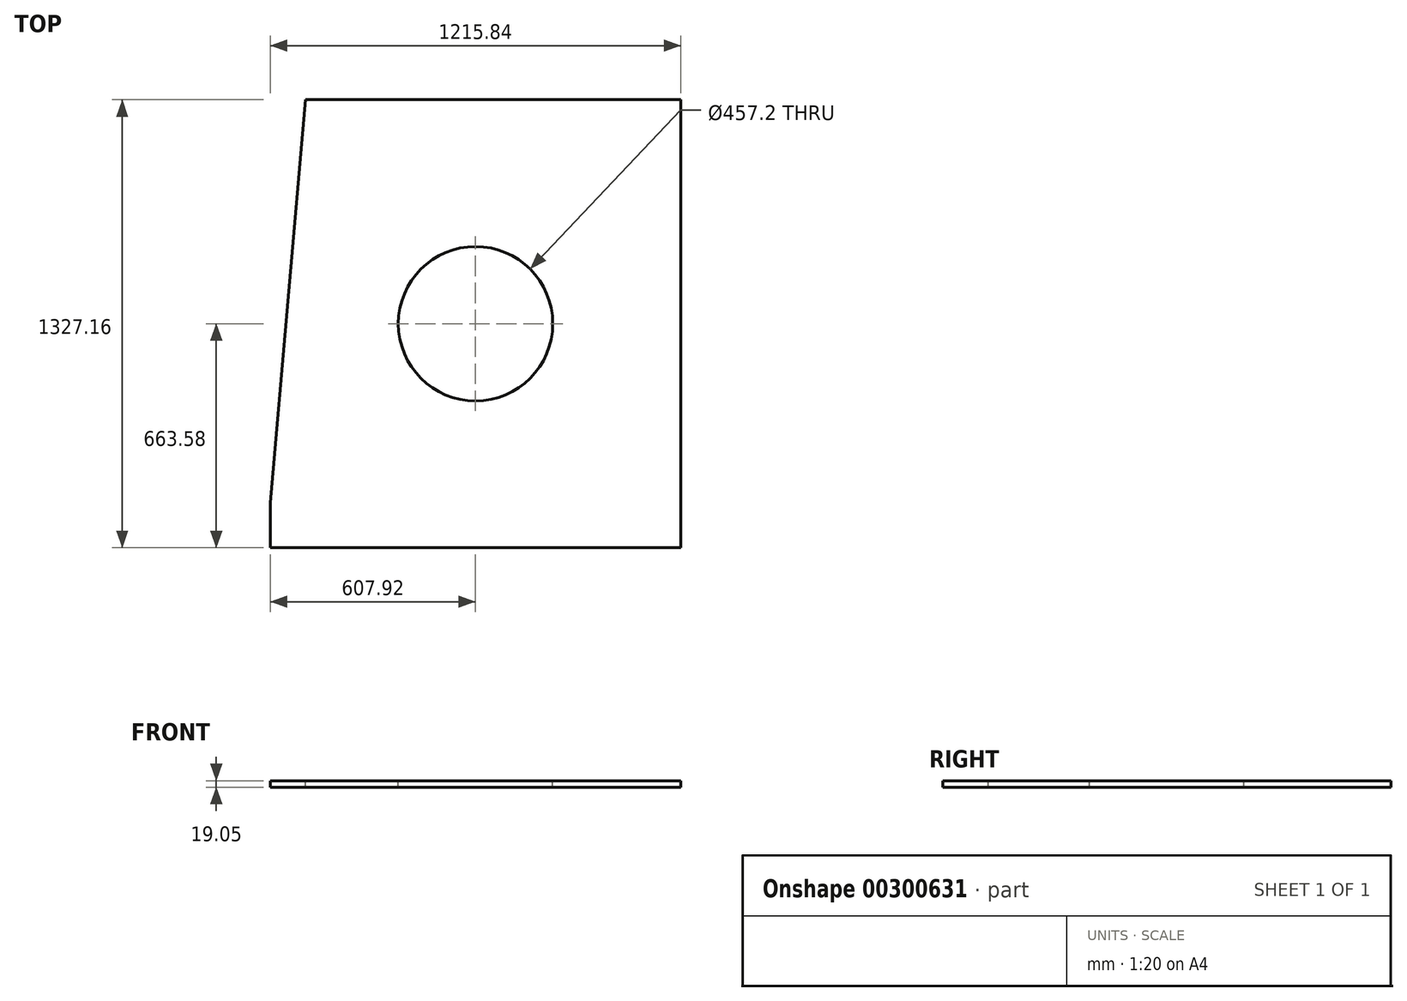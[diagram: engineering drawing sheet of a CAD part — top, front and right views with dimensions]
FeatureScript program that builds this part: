
annotation { "Feature Type Name" : "Feature", "Feature Type Description" : "" }
export const myFeature = defineFeature(function(context is Context, id is Id, definition is map)
    precondition{}
    {
        {
            var Q0;
            Q0=qCreatedBy(makeId("Top.planeOp"),FACE);
            var sketch = newSketch(context, id + "F0", { "sketchPlane" : qUnion([Q0])});
            skLineSegment(sketch, "E0.bottom", {"start": v(-607.92, -663.58) * mm, "end": v(607.92, -663.58) * mm});
            skLineSegment(sketch, "E0.top", {"start": v(-607.92, 663.58) * mm, "end": v(607.92, 663.58) * mm});
            skLineSegment(sketch, "E0.left", {"start": v(-607.92, -663.58) * mm, "end": v(-607.92, 663.58) * mm});
            skLineSegment(sketch, "E0.right", {"start": v(607.92, -663.58) * mm, "end": v(607.92, 663.58) * mm});
            skPoint(sketch, "E0.middle", {"position": v(0, 0) * mm});
            skSolve(sketch);
        }
        {
            var Q0;
            Q0=qSketchRegion(id+"F0",true);
            extrude(context, id + "F1", {"entities" : qUnion([Q0]), "depth" : 19.05 * mm});
        }
        {
            var Q0;
            Q0=makeQuery(id+"F1.opExtrude","SWEPT_EDGE",EDGE,{"disambiguationData":[OSD([sQuery(id+"F0.wireOp",EDGE,"E0.top"),sQuery(id+"F0.wireOp",EDGE,"E0.left")])]});
            chamfer(context, id + "F2", {"entities" : qUnion([Q0]), "chamferType" : ChamferType.OFFSET_ANGLE, "width" : 1193.52 * mm, "oppositeDirection" : true, "angle" : 5 * degree, "tangentPropagation" : true});
        }
        {
            var Q0;
            Q0=makeQuery(id+"F1.opExtrude","CAP_FACE",FACE,{"disambiguationData":[OSD([sQuery(id+"F0.wireOp",EDGE,"E0.bottom"),sQuery(id+"F0.wireOp",EDGE,"E0.top"),sQuery(id+"F0.wireOp",EDGE,"E0.left"),sQuery(id+"F0.wireOp",EDGE,"E0.right")])],"isStart":false});
            var sketch = newSketch(context, id + "F3", { "sketchPlane" : qUnion([Q0])});
            skCircle(sketch, "E1", {"center": v(0, 0) * mm, "radius": 228.6 * mm});
            skSolve(sketch);
        }
        {
            var Q0;
            Q0 = qSketchRegion(id + "F3", true);
            extrude(context, id + "F4", {"entities" : qUnion([Q0]), "operationType" : NewBodyOperationType.REMOVE, "endBound" : BoundingType.THROUGH_ALL, "oppositeDirection" : true, "depth" : 25.4 * mm});
        }
    });
